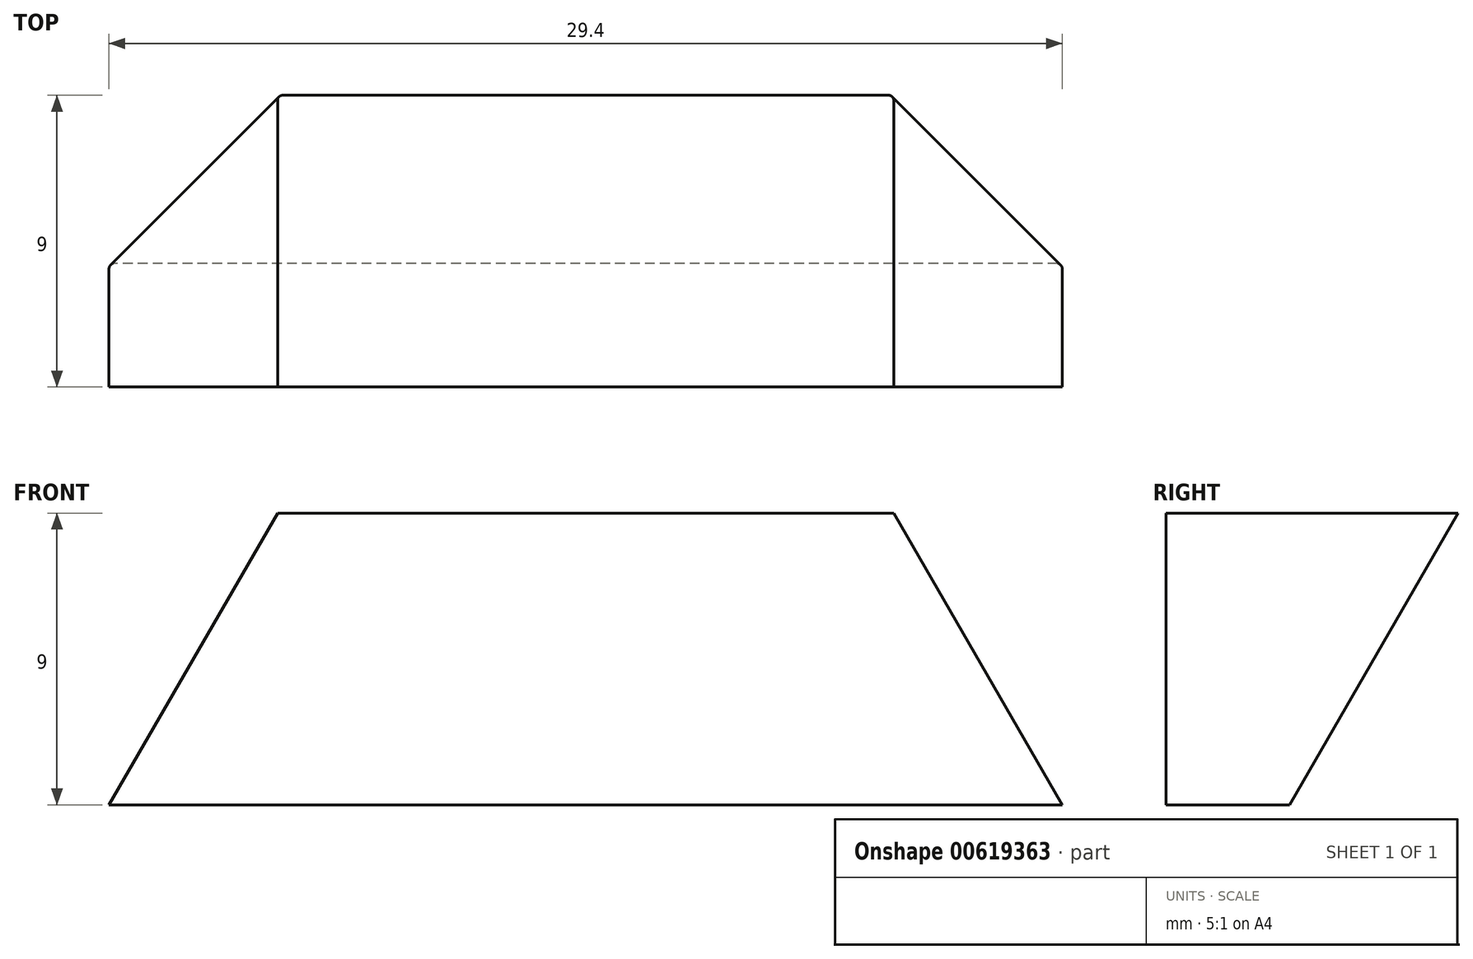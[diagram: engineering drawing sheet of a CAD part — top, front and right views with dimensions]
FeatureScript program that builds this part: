
annotation { "Feature Type Name" : "Feature", "Feature Type Description" : "" }
export const myFeature = defineFeature(function(context is Context, id is Id, definition is map)
    precondition{}
    {
        {
            assignVariable(context, id + "F0", {"name" : "x2", "anyValue" : 20});
        }
        {
            assignVariable(context, id + "F1", {"name" : "filletr", "anyValue" : .1});
        }
        {
            assignVariable(context, id + "F2", {"name" : "slotwidth", "anyValue" : 2});
        }
        {
            assignVariable(context, id + "F3", {"name" : "sliderlength", "anyValue" : (getVariable(context, 'x2') - getVariable(context, 'slotwidth')) / 2});
        }
        {
            assignVariable(context, id + "F4", {"name" : "holedepth", "anyValue" : .5});
        }
        {
            var Q0;
            Q0=qCreatedBy(makeId("Front.planeOp"),FACE);
            var sketch = newSketch(context, id + "F5", { "sketchPlane" : qUnion([Q0])});
            skLineSegment(sketch, "E0", {"start": v(9.5, 9) * mm, "end": v(14.7, 0) * mm});
            skLineSegment(sketch, "E1", {"start": v(14.7, 0) * mm, "end": v(-14.7, 0) * mm});
            skLineSegment(sketch, "E2", {"start": v(-14.7, 0) * mm, "end": v(-9.5, 9) * mm});
            skLineSegment(sketch, "E3", {"start": v(-9.5, 9) * mm, "end": v(9.5, 9) * mm});
            skLineSegment(sketch, "E4", {"start": v(0, 0) * mm, "end": v(0, 29.38) * mm, "construction": true});
            skSolve(sketch);
        }
        {
            var Q0;
            Q0=makeQuery(id+"F5.imprint","IMPRINT",FACE,{"disambiguationData":[TD([[makeQuery(id+"F5.imprint","IMPRINT",EDGE,{"derivedFrom":sQuery(id+"F5.wireOp",EDGE,"E0")}),-1.0]])]});
            extrude(context, id + "F6", {"entities" : qUnion([Q0]), "depth" : (getVariable(context, 'sliderlength')) * mm, "offsetDistance" : 25 * mm});
        }
        {
            var Q0;
            Q0=makeQuery(id+"F6.opExtrude","SWEPT_FACE",FACE,{"disambiguationData":[OSD([sQuery(id+"F5.wireOp",EDGE,"E3")])]});
            var sketch = newSketch(context, id + "F7", { "sketchPlane" : qUnion([Q0])});
            skLineSegment(sketch, "E5", {"start": v(-9.5, -45) * mm, "end": v(9.5, -45) * mm, "construction": true});
            skLineSegment(sketch, "E6", {"start": v(0, 0) * mm, "end": v(0, -90) * mm, "construction": true});
            skPoint(sketch, "E7", {"position": v(0, -45) * mm});
            skCircle(sketch, "E8", {"center": v(0, -45) * mm, "radius": 2.5 * mm});
            skSolve(sketch);
        }
        {
            var Q0;
            Q0=makeQuery(id+"F7.imprint","IMPRINT",FACE,{"disambiguationData":[TD([[makeQuery(id+"F7.imprint","IMPRINT",EDGE,{"derivedFrom":sQuery(id+"F7.wireOp",EDGE,"E8")}),1.0]])]});
            extrude(context, id + "F8", {"entities" : qUnion([Q0]), "operationType" : NewBodyOperationType.REMOVE, "oppositeDirection" : true, "depth" : (getVariable(context, 'holedepth')) * mm, "offsetDistance" : 25 * mm});
        }
        {
            var Q0;
            Q0=qCreatedBy(makeId("Right.planeOp"),FACE);
            var sketch = newSketch(context, id + "F9", { "sketchPlane" : qUnion([Q0])});
            skLineSegment(sketch, "E9", {"start": v(0, 9) * mm, "end": v(0, 0) * mm});
            skLineSegment(sketch, "E10", {"start": v(0, 0) * mm, "end": v(-5.2, 0) * mm});
            skLineSegment(sketch, "E11", {"start": v(-5.2, 0) * mm, "end": v(0, 9) * mm});
            skLineSegment(sketch, "E12", {"start": v(-90, 9) * mm, "end": v(-90, 0) * mm});
            skLineSegment(sketch, "E13", {"start": v(-90, 0) * mm, "end": v(-84.8, 0) * mm});
            skLineSegment(sketch, "E14", {"start": v(-84.8, 0) * mm, "end": v(-90, 9) * mm});
            skSolve(sketch);
        }
        {
            var Q0;
            Q0=qSketchRegion(id+"F9",true);
            extrude(context, id + "F10", {"entities" : qUnion([Q0]), "operationType" : NewBodyOperationType.REMOVE, "endBound" : BoundingType.THROUGH_ALL, "depth" : 100 * mm, "offsetDistance" : 25 * mm, "hasSecondDirection" : true, "secondDirectionBound" : BoundingType.THROUGH_ALL, "secondDirectionOppositeDirection" : true, "secondDirectionDepth" : 25 * mm});
        }
        {
            var Q0;
            Q0=makeQuery(id+"F10.boolean.opBoolean","INTERSECT",EDGE,{"derivedFrom":[makeQuery(id+"F6.opExtrude","SWEPT_FACE",FACE,{"disambiguationData":[OSD([sQuery(id+"F5.wireOp",EDGE,"E2")])]}),makeQuery(id+"F10.opExtrude","SWEPT_FACE",FACE,{"disambiguationData":[OSD([sQuery(id+"F9.wireOp",EDGE,"E14")])]})]});
            var Q1;
            Q1=makeQuery(id+"F10.boolean.opBoolean","INTERSECT",EDGE,{"derivedFrom":[makeQuery(id+"F6.opExtrude","SWEPT_FACE",FACE,{"disambiguationData":[OSD([sQuery(id+"F5.wireOp",EDGE,"E0")])]}),makeQuery(id+"F10.opExtrude","SWEPT_FACE",FACE,{"disambiguationData":[OSD([sQuery(id+"F9.wireOp",EDGE,"E14")])]})]});
            var Q2;
            Q2=makeQuery(id+"F10.boolean.opBoolean","INTERSECT",EDGE,{"derivedFrom":[makeQuery(id+"F6.opExtrude","SWEPT_FACE",FACE,{"disambiguationData":[OSD([sQuery(id+"F5.wireOp",EDGE,"E0")])]}),makeQuery(id+"F10.opExtrude","SWEPT_FACE",FACE,{"disambiguationData":[OSD([sQuery(id+"F9.wireOp",EDGE,"E11")])]})]});
            var Q3;
            Q3=makeQuery(id+"F10.boolean.opBoolean","INTERSECT",EDGE,{"derivedFrom":[makeQuery(id+"F6.opExtrude","SWEPT_FACE",FACE,{"disambiguationData":[OSD([sQuery(id+"F5.wireOp",EDGE,"E2")])]}),makeQuery(id+"F10.opExtrude","SWEPT_FACE",FACE,{"disambiguationData":[OSD([sQuery(id+"F9.wireOp",EDGE,"E11")])]})]});
            fillet(context, id + "F11", {"entities" : qUnion([Q0, Q1, Q2, Q3]), "radius" : (getVariable(context, 'filletr')) * mm, "tangentPropagation" : true, "allowEdgeOverflow" : false});
        }
    });
